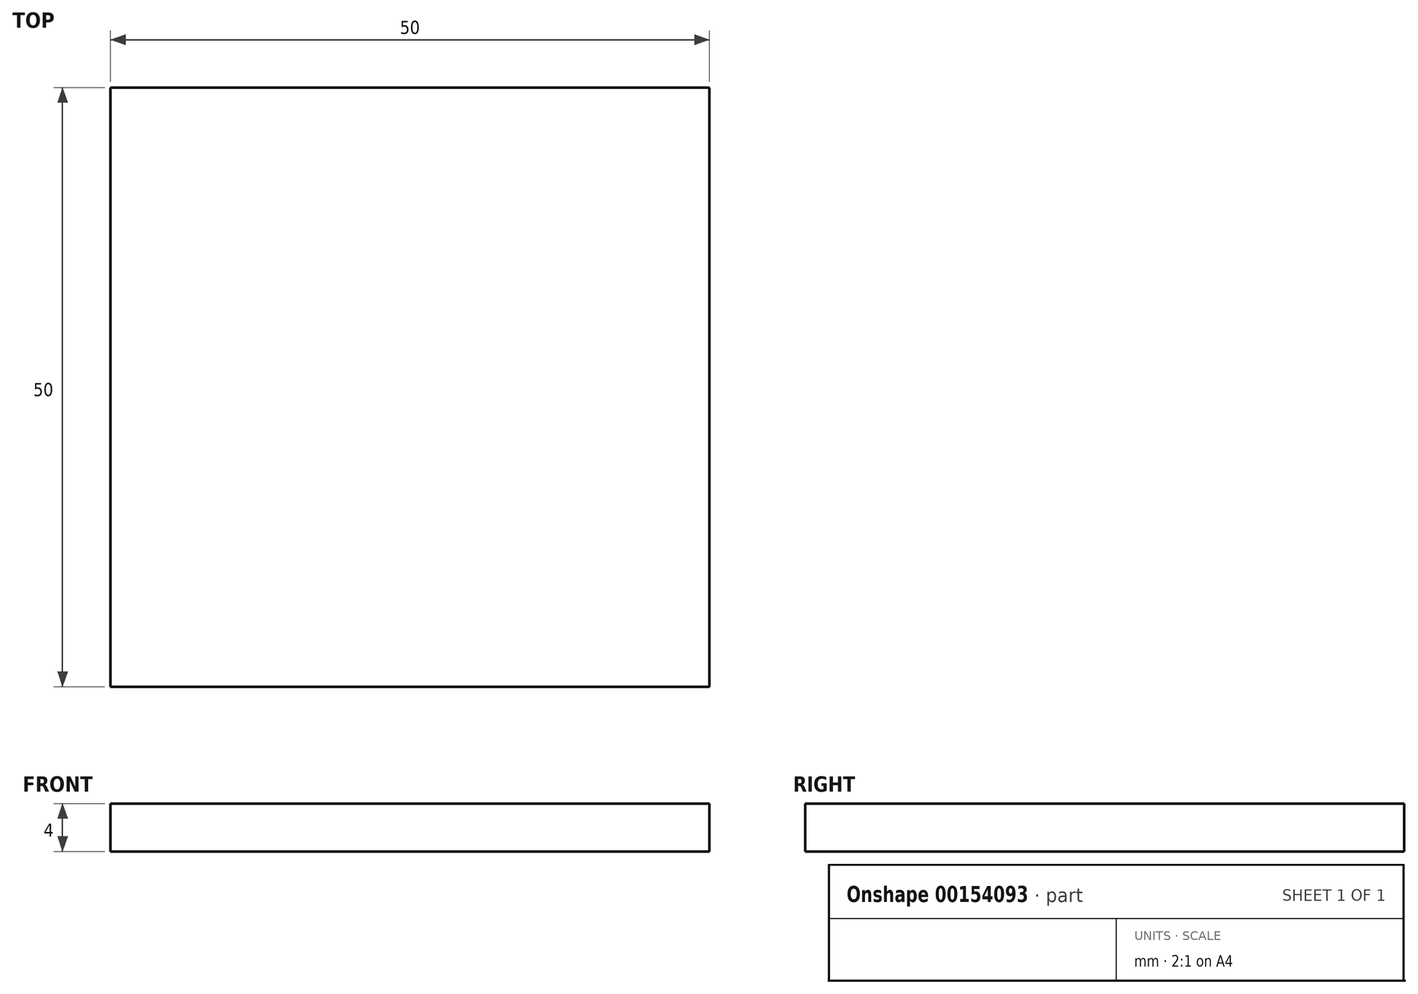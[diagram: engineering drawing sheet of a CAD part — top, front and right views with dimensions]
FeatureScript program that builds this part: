
annotation { "Feature Type Name" : "Feature", "Feature Type Description" : "" }
export const myFeature = defineFeature(function(context is Context, id is Id, definition is map)
    precondition{}
    {
        {
            var Q0;
            Q0=qCreatedBy(makeId("Top.planeOp"),FACE);
            var sketch = newSketch(context, id + "F0", { "sketchPlane" : qUnion([Q0])});
            skLineSegment(sketch, "E0.bottom", {"start": v(25, -25) * mm, "end": v(-25, -25) * mm});
            skLineSegment(sketch, "E0.top", {"start": v(25, 25) * mm, "end": v(-25, 25) * mm});
            skLineSegment(sketch, "E0.left", {"start": v(25, -25) * mm, "end": v(25, 25) * mm});
            skLineSegment(sketch, "E0.right", {"start": v(-25, -25) * mm, "end": v(-25, 25) * mm});
            skPoint(sketch, "E0.middle", {"position": v(0, 0) * mm});
            skSolve(sketch);
        }
        {
            var Q0;
            Q0=makeQuery(id+"F0.imprint","IMPRINT",FACE,{"disambiguationData":[TD([[makeQuery(id+"F0.imprint","IMPRINT",EDGE,{"derivedFrom":sQuery(id+"F0.wireOp",EDGE,"E0.bottom")}),-1.0]])]});
            extrude(context, id + "F1", {"entities" : qUnion([Q0]), "depth" : 4 * mm});
        }
    });
